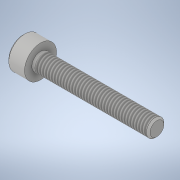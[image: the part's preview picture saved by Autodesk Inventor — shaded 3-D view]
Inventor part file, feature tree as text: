
AUTODESK INVENTOR PART (.ipt)
format: ipt  version: 2022 (Build 260153000, 153)  size: 151,040 bytes
history: native  units: mm
features: other x14, sketch x3, revolve x1, thread x1, hole x1, extrude x1
ambient origin geometry x8: Origin, YZ Plane, XZ Plane, XY Plane, X Axis, Y Axis, Z Axis, Center Point
bodies: Solid1 (feature_tree)
feature tree (21):
  revolve  "Revolution1"  [1 undecoded]
  thread  "Thread1"  [1 undecoded]
  hole  "Hole1"  [1 undecoded]
  extrude  "Extrusion1"  [1 undecoded]
  other  "bolt_XY"
  other  "bolt_YZ"
  other  "bolt_ZX"
  other  "bolt_X"
  other  "bolt_Y"
  other  "bolt_Z"
  other  "bolt_Center"
  other  "nut_XY"
  other  "nut_YZ"
  other  "nut_ZX"
  other  "nut_X"
  other  "nut_Y"
  other  "nut_Z"
  other  "nut_Center"
  sketch  "Sketch_1"  dims[d0=360.0deg d1=19.5mm d2=0.5mm]
  sketch  "Sketch2"  dims[d3=2.5mm d4=6.0mm d5=4.0mm d6=2.0mm d7=90.0deg d8=1.3mm d9=120.0deg d10=1.3mm d11=0.0mm]
  sketch  "Sketch_3"  dims[d12=0.0mm d13=0.0mm]
note: 4 required parameter values undecoded (feature->parameter linkage not recoverable at this tier; creation-order binding heuristic only, values carry confidence <= 0.55)